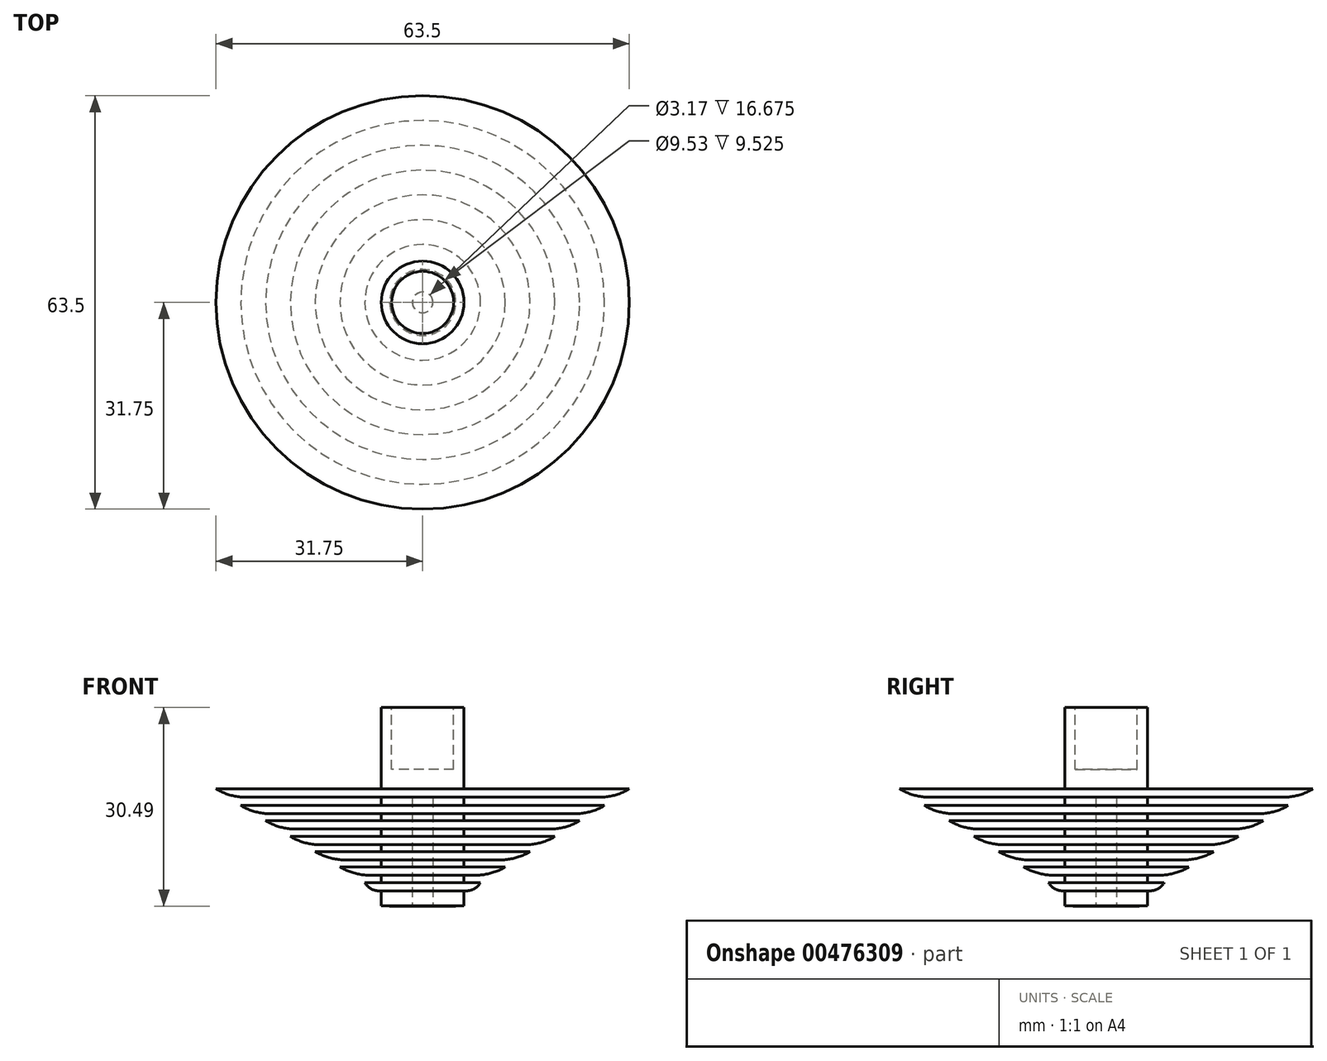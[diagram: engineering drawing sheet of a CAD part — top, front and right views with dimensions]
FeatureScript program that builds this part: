
annotation { "Feature Type Name" : "Feature", "Feature Type Description" : "" }
export const myFeature = defineFeature(function(context is Context, id is Id, definition is map)
    precondition{}
    {
        {
            var Q0;
            Q0=qCreatedBy(makeId("Front.planeOp"),FACE);
            var sketch = newSketch(context, id + "F0", { "sketchPlane" : qUnion([Q0])});
            skLineSegment(sketch, "E0.bottom", {"start": v(0, 0) * mm, "end": v(6.35, 0) * mm});
            skLineSegment(sketch, "E0.top", {"start": v(0, 30.48) * mm, "end": v(6.35, 30.48) * mm});
            skLineSegment(sketch, "E0.left", {"start": v(0, 0) * mm, "end": v(0, 30.48) * mm});
            skLineSegment(sketch, "E0.right", {"start": v(6.35, 0) * mm, "end": v(6.35, 30.48) * mm});
            skLineSegment(sketch, "E1.bottom", {"start": v(0, 0) * mm, "end": v(5.08, 0) * mm});
            skLineSegment(sketch, "E1.top", {"start": v(0, 1.26) * mm, "end": v(5.08, 1.26) * mm});
            skLineSegment(sketch, "E1.left", {"start": v(0, 0) * mm, "end": v(0, 1.26) * mm});
            skLineSegment(sketch, "E1.right", {"start": v(5.08, 0) * mm, "end": v(5.08, 1.26) * mm});
            skLineSegment(sketch, "E2.bottom", {"start": v(0, 2.33) * mm, "end": v(8.9, 2.33) * mm});
            skLineSegment(sketch, "E2.top", {"start": v(0, 3.6) * mm, "end": v(8.89, 3.6) * mm});
            skLineSegment(sketch, "E2.left", {"start": v(0, 2.33) * mm, "end": v(0, 3.6) * mm});
            skLineSegment(sketch, "E2.right", {"start": v(8.9, 2.33) * mm, "end": v(8.9, 3.6) * mm});
            skLineSegment(sketch, "E3.bottom", {"start": v(0, 4.73) * mm, "end": v(12.7, 4.73) * mm});
            skLineSegment(sketch, "E3.top", {"start": v(0, 6) * mm, "end": v(12.7, 6) * mm});
            skLineSegment(sketch, "E3.left", {"start": v(0, 4.73) * mm, "end": v(0, 6) * mm});
            skLineSegment(sketch, "E3.right", {"start": v(12.7, 4.73) * mm, "end": v(12.7, 6) * mm});
            skLineSegment(sketch, "E4.bottom", {"start": v(0, 7.09) * mm, "end": v(16.51, 7.09) * mm});
            skLineSegment(sketch, "E4.top", {"start": v(0, 8.36) * mm, "end": v(16.51, 8.36) * mm});
            skLineSegment(sketch, "E4.left", {"start": v(0, 7.09) * mm, "end": v(0, 8.36) * mm});
            skLineSegment(sketch, "E4.right", {"start": v(16.51, 7.09) * mm, "end": v(16.51, 8.36) * mm});
            skLineSegment(sketch, "E5.bottom", {"start": v(0, 9.41) * mm, "end": v(20.32, 9.41) * mm});
            skLineSegment(sketch, "E5.top", {"start": v(0, 10.68) * mm, "end": v(20.32, 10.68) * mm});
            skLineSegment(sketch, "E5.left", {"start": v(0, 9.41) * mm, "end": v(0, 10.68) * mm});
            skLineSegment(sketch, "E5.right", {"start": v(20.32, 9.41) * mm, "end": v(20.32, 10.68) * mm});
            skLineSegment(sketch, "E6.bottom", {"start": v(0, 11.83) * mm, "end": v(24.13, 11.83) * mm});
            skLineSegment(sketch, "E6.top", {"start": v(0, 13.1) * mm, "end": v(24.13, 13.1) * mm});
            skLineSegment(sketch, "E6.left", {"start": v(0, 11.83) * mm, "end": v(0, 13.1) * mm});
            skLineSegment(sketch, "E6.right", {"start": v(24.13, 11.83) * mm, "end": v(24.13, 13.1) * mm});
            skLineSegment(sketch, "E7.bottom", {"start": v(0, 14.17) * mm, "end": v(27.94, 14.17) * mm});
            skLineSegment(sketch, "E7.top", {"start": v(0, 15.44) * mm, "end": v(27.94, 15.44) * mm});
            skLineSegment(sketch, "E7.left", {"start": v(0, 14.17) * mm, "end": v(0, 15.44) * mm});
            skLineSegment(sketch, "E7.right", {"start": v(27.94, 14.17) * mm, "end": v(27.94, 15.44) * mm});
            skLineSegment(sketch, "E8.bottom", {"start": v(0, 16.72) * mm, "end": v(31.75, 16.72) * mm});
            skLineSegment(sketch, "E8.top", {"start": v(0, 17.99) * mm, "end": v(31.75, 17.99) * mm});
            skLineSegment(sketch, "E8.left", {"start": v(0, 16.72) * mm, "end": v(0, 17.99) * mm});
            skLineSegment(sketch, "E8.right", {"start": v(31.75, 16.72) * mm, "end": v(31.75, 17.99) * mm});
            skSolve(sketch);
        }
        {
            var Q0;
            Q0 = qSketchRegion(id + "F0", true);
            var Q1;
            Q1=sQuery(id+"F0.wireOp",EDGE,"E0.left");
            revolve(context, id + "F1", {"entities" : qUnion([Q0]), "axis" : qUnion([Q1]), "revolveType" : RevolveType.FULL});
        }
        {
            var Q0;
            Q0=qCreatedBy(makeId("Top.planeOp"),FACE);
            var sketch = newSketch(context, id + "F2", { "sketchPlane" : qUnion([Q0])});
            skCircle(sketch, "E9", {"center": v(0, 0) * mm, "radius": 1.59 * mm});
            skSolve(sketch);
        }
        {
            var Q0;
            Q0 = qSketchRegion(id + "F2", true);
            extrude(context, id + "F3", {"entities" : qUnion([Q0]), "operationType" : NewBodyOperationType.REMOVE, "depth" : 16.67 * mm, "offsetDistance" : 25.4 * mm});
        }
        {
            var Q0;
            Q0=makeQuery(id+"F1.opRevolve","SWEPT_FACE",FACE,{"disambiguationData":[OSD([sQuery(id+"F0.wireOp",EDGE,"E0.top")])]});
            var sketch = newSketch(context, id + "F4", { "sketchPlane" : qUnion([Q0])});
            skCircle(sketch, "E10", {"center": v(0, 0) * mm, "radius": 4.76 * mm});
            skSolve(sketch);
        }
        {
            var Q0;
            Q0 = qSketchRegion(id + "F4", true);
            extrude(context, id + "F5", {"entities" : qUnion([Q0]), "operationType" : NewBodyOperationType.REMOVE, "oppositeDirection" : true, "depth" : 9.52 * mm});
        }
        {
            var Q0;
            Q0=makeQuery(id+"F1.opRevolve","SWEPT_EDGE",EDGE,{"disambiguationData":[OSD([sQuery(id+"F0.wireOp",EDGE,"E8.bottom"),sQuery(id+"F0.wireOp",EDGE,"E8.right")])]});
            var Q1;
            Q1=makeQuery(id+"F1.opRevolve","SWEPT_EDGE",EDGE,{"disambiguationData":[OSD([sQuery(id+"F0.wireOp",EDGE,"E7.bottom"),sQuery(id+"F0.wireOp",EDGE,"E7.right")])]});
            var Q2;
            Q2=makeQuery(id+"F1.opRevolve","SWEPT_EDGE",EDGE,{"disambiguationData":[OSD([sQuery(id+"F0.wireOp",EDGE,"E6.bottom"),sQuery(id+"F0.wireOp",EDGE,"E6.right")])]});
            var Q3;
            Q3=makeQuery(id+"F1.opRevolve","SWEPT_EDGE",EDGE,{"disambiguationData":[OSD([sQuery(id+"F0.wireOp",EDGE,"E5.bottom"),sQuery(id+"F0.wireOp",EDGE,"E5.right")])]});
            var Q4;
            Q4=makeQuery(id+"F1.opRevolve","SWEPT_EDGE",EDGE,{"disambiguationData":[OSD([sQuery(id+"F0.wireOp",EDGE,"E4.bottom"),sQuery(id+"F0.wireOp",EDGE,"E4.right")])]});
            var Q5;
            Q5=makeQuery(id+"F1.opRevolve","SWEPT_EDGE",EDGE,{"disambiguationData":[OSD([sQuery(id+"F0.wireOp",EDGE,"E3.bottom"),sQuery(id+"F0.wireOp",EDGE,"E3.right")])]});
            fillet(context, id + "F6", {"entities" : qUnion([Q0, Q1, Q2, Q3, Q4, Q5]), "radius" : 8.9 * mm, "tangentPropagation" : true, "allowEdgeOverflow" : false});
        }
        {
            var Q0;
            Q0=makeQuery(id+"F1.opRevolve","SWEPT_EDGE",EDGE,{"disambiguationData":[OSD([sQuery(id+"F0.wireOp",EDGE,"E2.bottom"),sQuery(id+"F0.wireOp",EDGE,"E2.right")])]});
            fillet(context, id + "F7", {"entities" : qUnion([Q0]), "radius" : 2.54 * mm, "tangentPropagation" : true, "allowEdgeOverflow" : false});
        }
    });
